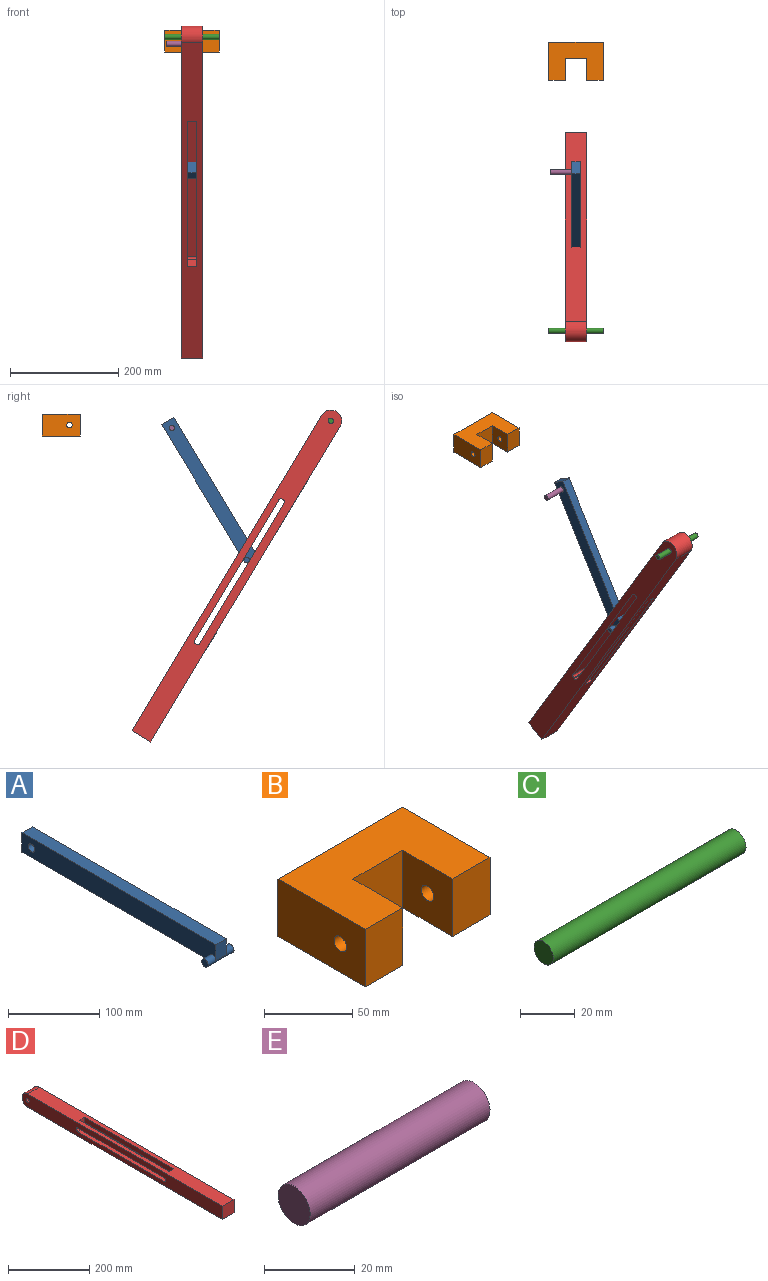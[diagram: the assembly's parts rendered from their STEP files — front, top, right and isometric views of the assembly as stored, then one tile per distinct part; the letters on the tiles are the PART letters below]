
ASSEMBLY  parts=5 mates=3
PART A: 10 faces, bbox 40x300x26 mm
  f0: plane 21x16mm, normal (0,-1,0), area 336mm2, adj f1,f3,f5,f6
  f1: plane 300x26mm, normal (1,0,0), area 7637.6mm2, adj f0,f2,f4,f5,f6,f9
  f2: plane 26x16mm, normal (0,1,0), area 416mm2, adj f1,f3,f4,f5
  f3: plane 300x26mm, normal (-1,0,0), area 7637.6mm2, adj f0,f2,f4,f5,f6,f9
  f4: plane 295x16mm, normal (0,0,-1), area 4720mm2, adj f1,f2,f3,f6
  f5: plane 300x16mm, normal (0,0,1), area 4800mm2, adj f0,f1,f2,f3
  f6: cylinder r=5mm len=40mm, axis (-1,0,0), area 879.6mm2, adj f0,f1,f3,f4,f7,f8
  f7: plane 10x10mm, normal (-1,0,0), area 78.5mm2, adj f6
  f8: plane 10x10mm, normal (1,0,0), area 78.5mm2, adj f6
  f9: cylinder r=5mm len=16mm, axis (1,0,0), area 502.7mm2, adj f1,f3
PART B: 12 faces, bbox 100x70x40 mm
  f0: plane 40x40mm, normal (0,-1,0), area 1600mm2, adj f1,f7,f8,f9
  f1: plane 40x40mm, normal (-1,0,0), area 1521.5mm2, adj f0,f2,f8,f9,f11
  f2: plane 40x30mm, normal (0,-1,0), area 1200mm2, adj f1,f3,f8,f9
  f3: plane 70x40mm, normal (1,0,0), area 2721.5mm2, adj f2,f4,f8,f9,f11
  f4: plane 100x40mm, normal (0,1,0), area 4000mm2, adj f3,f5,f8,f9
  f5: plane 70x40mm, normal (-1,0,0), area 2721.5mm2, adj f4,f6,f8,f9,f10
  f6: plane 40x30mm, normal (0,-1,0), area 1200mm2, adj f5,f7,f8,f9
  f7: plane 40x40mm, normal (1,0,0), area 1521.5mm2, adj f0,f6,f8,f9,f10
  f8: plane 100x70mm, normal (0,0,1), area 5400mm2, adj f0,f1,f2,f3,f4,f5,f6,f7
  f9: plane 100x70mm, normal (0,0,-1), area 5400mm2, adj f0,f1,f2,f3,f4,f5,f6,f7
  f10: cylinder r=5mm len=30mm, axis (-1,0,0), area 942.5mm2, adj f5,f7
  f11: cylinder r=5mm len=30mm, axis (-1,0,0), area 942.5mm2, adj f1,f3
PART C: 3 faces, bbox 100x10x10 mm
  f0: cylinder r=5mm len=100mm, axis (-1,0,0), area 3141.6mm2, adj f1,f2
  f1: plane 10x10mm, normal (1,0,0), area 78.5mm2, adj f0
  f2: plane 10x10mm, normal (-1,0,0), area 78.5mm2, adj f0
PART D: 20 faces, bbox 40x700x40 mm
  f0: plane 700x40mm, normal (1,0,0), area 24339.2mm2, adj f2,f3,f4,f5,f6,f7,f9,f11
  f1: plane 700x40mm, normal (-1,0,0), area 24339.2mm2, adj f2,f3,f4,f5,f6,f7,f9,f12
  f2: plane 680x40mm, normal (0,0,1), area 21896mm2, adj f0,f1,f4,f6,f7,f8,f9,f10
  f3: plane 680x40mm, normal (0,0,-1), area 27200mm2, adj f0,f1,f4,f6
  f4: plane 40x40mm, normal (0,-1,0), area 1600mm2, adj f0,f1,f2,f3
  f5: cylinder r=5mm len=40mm, axis (-1,0,0), area 1256.6mm2, adj f0,f1
  f6: cylinder r=20mm len=40mm, axis (1,0,0), area 2513.3mm2, adj f0,f1,f2,f3
  f7: plane 40x22mm, normal (0,1,0), area 397mm2, adj f0,f1,f2,f8,f10,f14,f16,f17
  f8: plane 312x21mm, normal (-1,0,0), area 5002.7mm2, adj f2,f7,f9,f11,f17,f18
  f9: plane 40x22mm, normal (0,-1,0), area 397mm2, adj f0,f1,f2,f8,f10,f15,f18,f19
  f10: plane 312x21mm, normal (1,0,0), area 5002.7mm2, adj f2,f7,f9,f13,f14,f15
  f11: plane 302x11.5mm, normal (0,0,-1), area 3473mm2, adj f0,f8,f17,f18
  f12: plane 302x40mm, normal (0,0,1), area 12080mm2, adj f0,f1,f16,f19
  f13: plane 302x11.5mm, normal (0,0,-1), area 3473mm2, adj f1,f10,f14,f15
  f14: cylinder r=5mm len=11.5mm, axis (-1,0,0), area 90.3mm2, adj f1,f7,f10,f13
  f15: cylinder r=5mm len=11.5mm, axis (1,0,0), area 90.3mm2, adj f1,f9,f10,f13
  f16: cylinder r=5mm len=40mm, axis (1,0,0), area 314.2mm2, adj f0,f1,f7,f12
  f17: cylinder r=5mm len=11.5mm, axis (-1,0,0), area 90.3mm2, adj f0,f7,f8,f11
  f18: cylinder r=5mm len=11.5mm, axis (1,0,0), area 90.3mm2, adj f0,f8,f9,f11
  f19: cylinder r=5mm len=40mm, axis (-1,0,0), area 314.2mm2, adj f0,f1,f9,f12
PART E: 3 faces, bbox 56x10x10 mm
  f0: cylinder r=5mm len=56mm, axis (-1,0,0), area 1759.3mm2, adj f1,f2
  f1: plane 10x10mm, normal (1,0,0), area 78.5mm2, adj f0
  f2: plane 10x10mm, normal (-1,0,0), area 78.5mm2, adj f0
PLACE A rot(axis=(1,0,0),58.9deg) t=(0,-91.87,176.12)mm
PLACE B at identity fixed
PLACE C t=(0,-482.68,8.06)mm
PLACE D rot(axis=(1,0,0),121deg) t=(0,-512.98,25.21)mm
PLACE E rot(axis=(-1,0,0),27deg) t=(-20,-20.17,-109.19)mm fixed
MATE revolute D.f6 <-> C.f0  axis (1,0,0) through (20,-502.68,8.06)mm
MATE revolute E.f0 <-> A.f9  axis (-1,0,0) through (8,-209.26,-5.04)mm
MATE pin_slot A.f6 <-> D.f14  axis (-1,0,0) through (-20,-347.1,-249.17)mm
